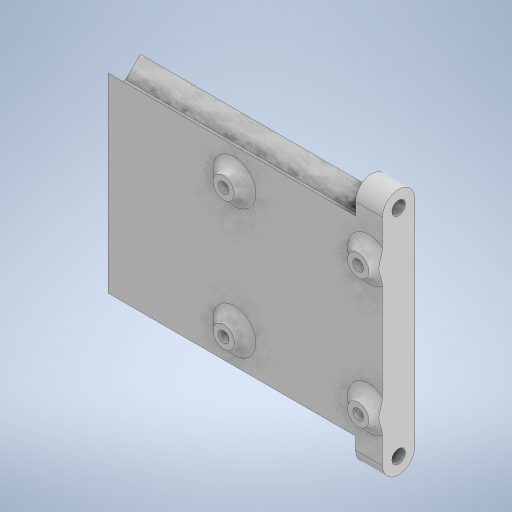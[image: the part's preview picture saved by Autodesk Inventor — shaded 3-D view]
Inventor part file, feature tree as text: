
AUTODESK INVENTOR PART (.ipt)
format: ipt  version: 2023 (Build 270158000, 158)  size: 342,016 bytes
history: native  units: mm
features: extrude x4, sketch x4, projected_geometry x2, other x1, fillet x1
ambient origin geometry x8: Origin, YZ Plane, XZ Plane, XY Plane, X Axis, Y Axis, Z Axis, Center Point
bodies: Body1 (feature_tree)
feature tree (12):
  other  "솔리드1"
  extrude  "돌출1"  Depth=51.0mm
  extrude  "돌출3"  Depth=30.0mm
  extrude  "돌출5"  Depth=2.0mm
  extrude  "돌출6"  Depth=15.0mm
  fillet  "모깎기1"  Radius=24.0mm
  sketch  "스케치1"
  sketch  "스케치4"
  projected_geometry  "투영된 루프1"
  sketch  "스케치6"
  projected_geometry  "투영된 루프2"
  sketch  "스케치7"
